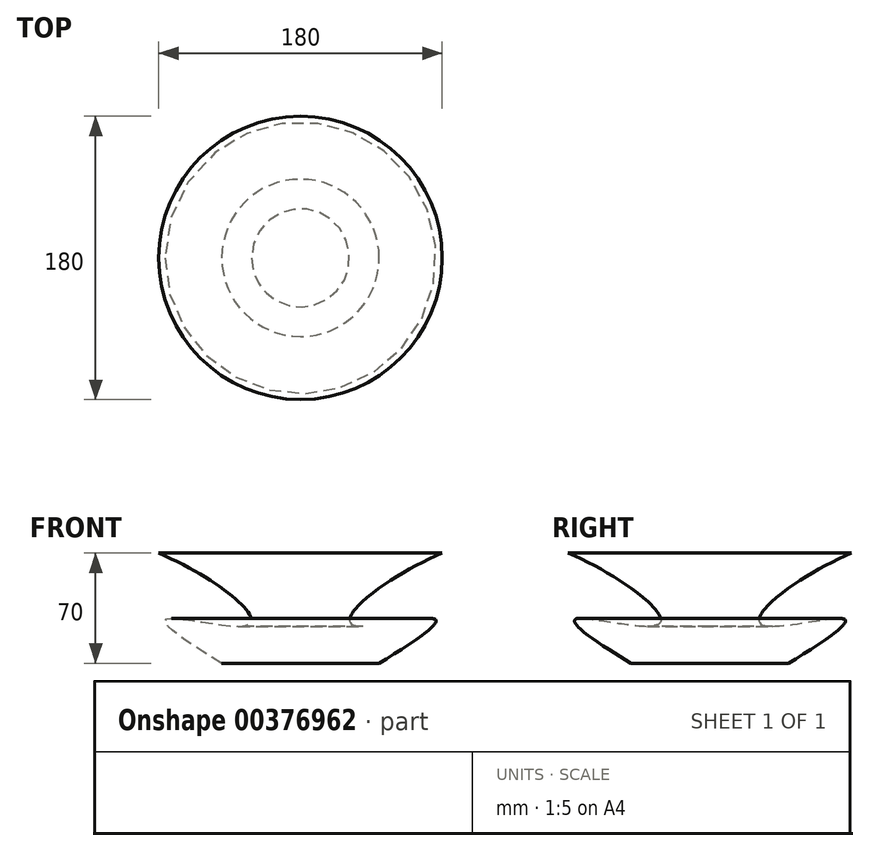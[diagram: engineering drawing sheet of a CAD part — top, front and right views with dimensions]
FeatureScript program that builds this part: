
annotation { "Feature Type Name" : "Feature", "Feature Type Description" : "" }
export const myFeature = defineFeature(function(context is Context, id is Id, definition is map)
    precondition{}
    {
        {
            var Q0;
            Q0=qCreatedBy(makeId("Front.planeOp"),FACE);
            var sketch = newSketch(context, id + "F0", { "sketchPlane" : qUnion([Q0])});
            skFitSpline(sketch, "E0", {"points": [v(50, 0) * mm, v(85.02, 28.16) * mm, v(33.1, 24.54) * mm, v(90, 70) * mm], "startDerivative": vector(209.07, 127.67) * mm, "endDerivative": vector(291.73, 125.13) * mm});
            skLineSegment(sketch, "E1", {"start": v(0, 0) * mm, "end": v(0, 92.73) * mm});
            skLineSegment(sketch, "E2", {"start": v(90, 70) * mm, "end": v(0, 70) * mm});
            skLineSegment(sketch, "E3", {"start": v(50, 0) * mm, "end": v(0, 0) * mm});
            skSolve(sketch);
        }
        {
            var Q0;
            Q0=makeQuery(id+"F0.imprint","IMPRINT",FACE,{"disambiguationData":[TD([[makeQuery(id+"F0.imprint","IMPRINT",EDGE,{"derivedFrom":sQuery(id+"F0.wireOp",EDGE,"E0")}),1.0]])]});
            var Q1;
            Q1=sQuery(id+"F0.wireOp",EDGE,"E1");
            revolve(context, id + "F1", {"entities" : qUnion([Q0]), "axis" : qUnion([Q1]), "revolveType" : RevolveType.FULL});
        }
    });
